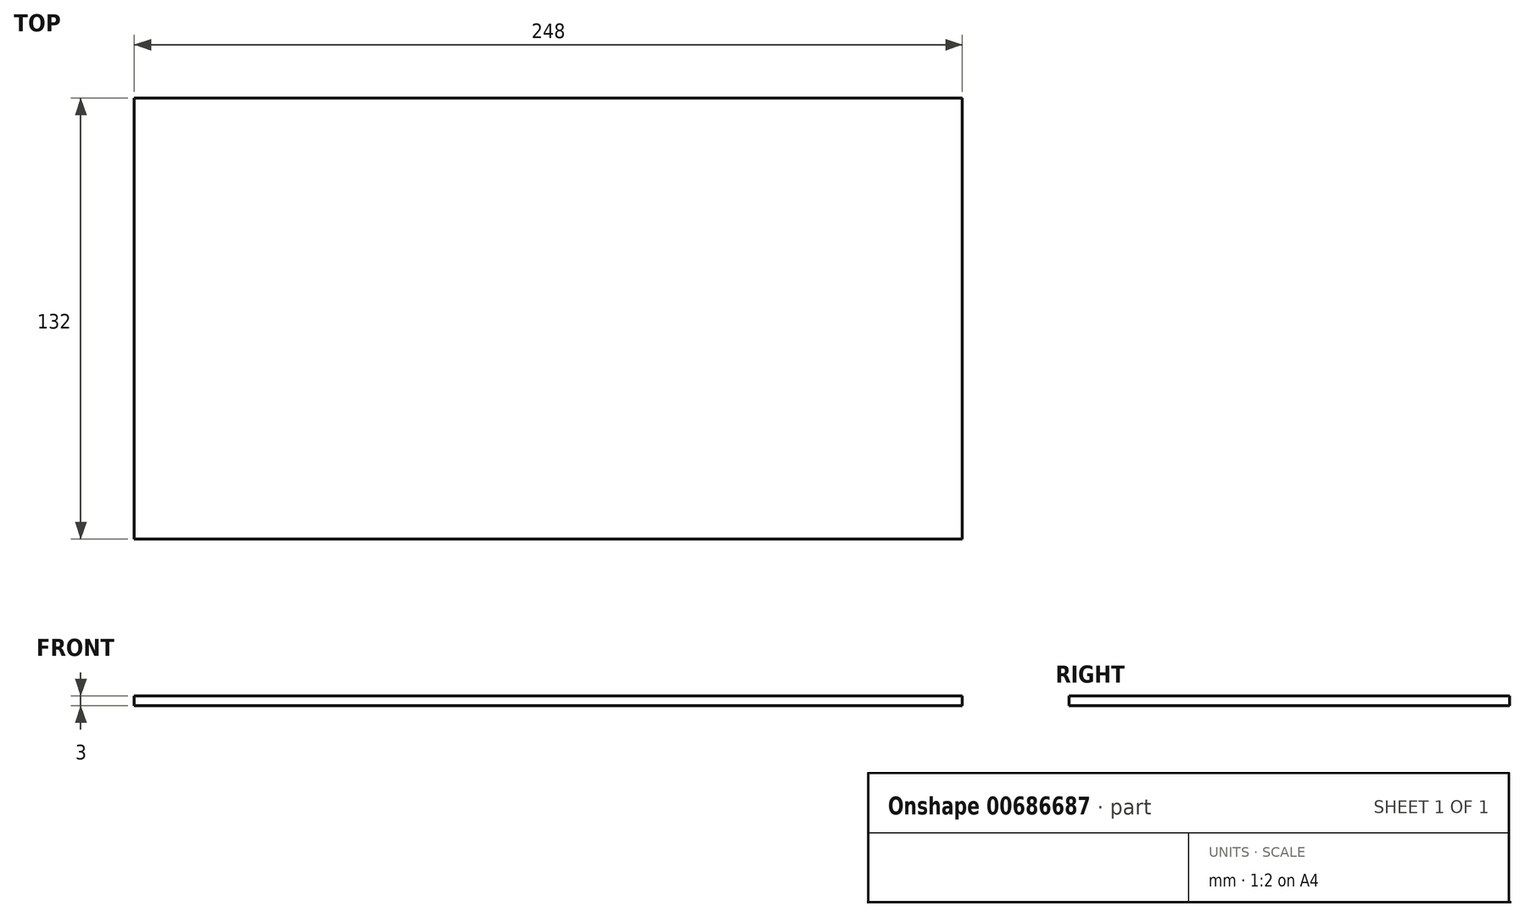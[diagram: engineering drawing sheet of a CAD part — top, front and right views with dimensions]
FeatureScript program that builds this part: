
annotation { "Feature Type Name" : "Feature", "Feature Type Description" : "" }
export const myFeature = defineFeature(function(context is Context, id is Id, definition is map)
    precondition{}
    {
        {
            var Q0;
            Q0=qCreatedBy(makeId("Top.planeOp"),FACE);
            var sketch = newSketch(context, id + "F0", { "sketchPlane" : qUnion([Q0])});
            skLineSegment(sketch, "E0.bottom", {"start": v(0, 0) * mm, "end": v(248, 0) * mm});
            skLineSegment(sketch, "E0.top", {"start": v(0, 132) * mm, "end": v(248, 132) * mm});
            skLineSegment(sketch, "E0.left", {"start": v(0, 0) * mm, "end": v(0, 132) * mm});
            skLineSegment(sketch, "E0.right", {"start": v(248, 0) * mm, "end": v(248, 132) * mm});
            skSolve(sketch);
        }
        {
            var Q0;
            Q0=makeQuery(id+"F0.imprint","IMPRINT",FACE,{"disambiguationData":[TD([[makeQuery(id+"F0.imprint","IMPRINT",EDGE,{"derivedFrom":sQuery(id+"F0.wireOp",EDGE,"E0.bottom")}),1.0]])]});
            extrude(context, id + "F1", {"entities" : qUnion([Q0]), "depth" : 3 * mm, "offsetDistance" : 25 * mm});
        }
    });
